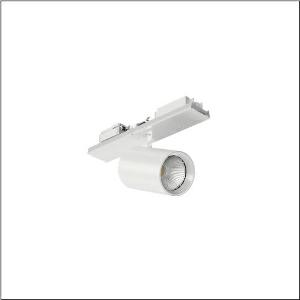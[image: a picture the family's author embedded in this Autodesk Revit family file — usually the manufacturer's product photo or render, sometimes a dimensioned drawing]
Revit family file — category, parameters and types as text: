
# Revit family: licross_r__spot_31_51sl12da45b_e1b3
name_source: partatom
category: Lighting Fixtures
units: mm (PartAtom-declared; Revit-internal decimal feet)

## family parameters
Cut with Voids When Loaded = No
Host = Face
Light Source = No
Part Type = Normal
Room Calculation Point = No
Round Connector Dimension = Use Diameter
Shared = No

## types (1)
- --- (1 x LED, 5140 lm, 43.9 W, 4000K)
    Apparent Load = 44 VA
    CIE Flux Codes = 93 97 99 100 100
    Color Rendering = 90
    Color Temperature = 4000K
    Default Elevation = 1800 mm
    Description = Licross® Spot 31, directional spotlight, light control with lens, of plastic, LED rated luminous flux: 5.140lm, light colour: 940, with plug, 5-pole, mains connection: 220..240V, AC, 50/60Hz, of aluminium, traffic white (RAL 9016), length: 140mm, diameter: 90mm, protection rating (complete): IP20, insulation class (complete): insulation class I (protective earthing), certification: CE, packaging unit: 1 piece
    Height = 175 mm
    Lamp = 1 x LED
    Lamp Light Flux = 5140 lm
    Lamp Power = 43.9 W
    Lamp count = 1
    Length = 90 mm
    Luminous efficacy = 117 lm/W
    Manufacturer = Siteco
    ModVariant = No
    Model = 51SL12DA45B
    Mounting Place = Ceiling
    Mounting Type = Pendant
    Number of Poles = 1
    OnlyDefault = Yes
    Power Factor = 1
    Product Name = Licross® Spot 31
    Product group = directional spotlight
    ProductGroupID = 905
    Protection Class = Protection class I
    Protection Degree = IP 20
    RLX_Detail_Level = 1
    RLX_Emergency_Light_Flux = 0 lm
    RLX_Emergency_Type = 0
    RLX_Emergency_Type_DB = No
    RlxData = <blob elided: 14817 chars, md5=11d9f10f>
    Socket = socket
    Standby Power = 0 W
    System Light Flux = 5140 lm
    System Power = 44 W
    Type Comments = factory setting: luminous flux: 100 % | (ON | ON | ON) | 1050 mA
    Type Image = l_1245720.jpg
    URL = http://relux.com
    VarID = @adj_063975
    Voltage = 0 V
    Weight = 0.00 kg
    Width = 0 mm  [stored 0 ft]

note: [stored X ft] marks values corroborated as IEEE doubles in the binary element streams (Revit-internal decimal feet)

## geometry (parser evidence)
native form markers: Sweep x11
no freeform markers — native parametric forms only
